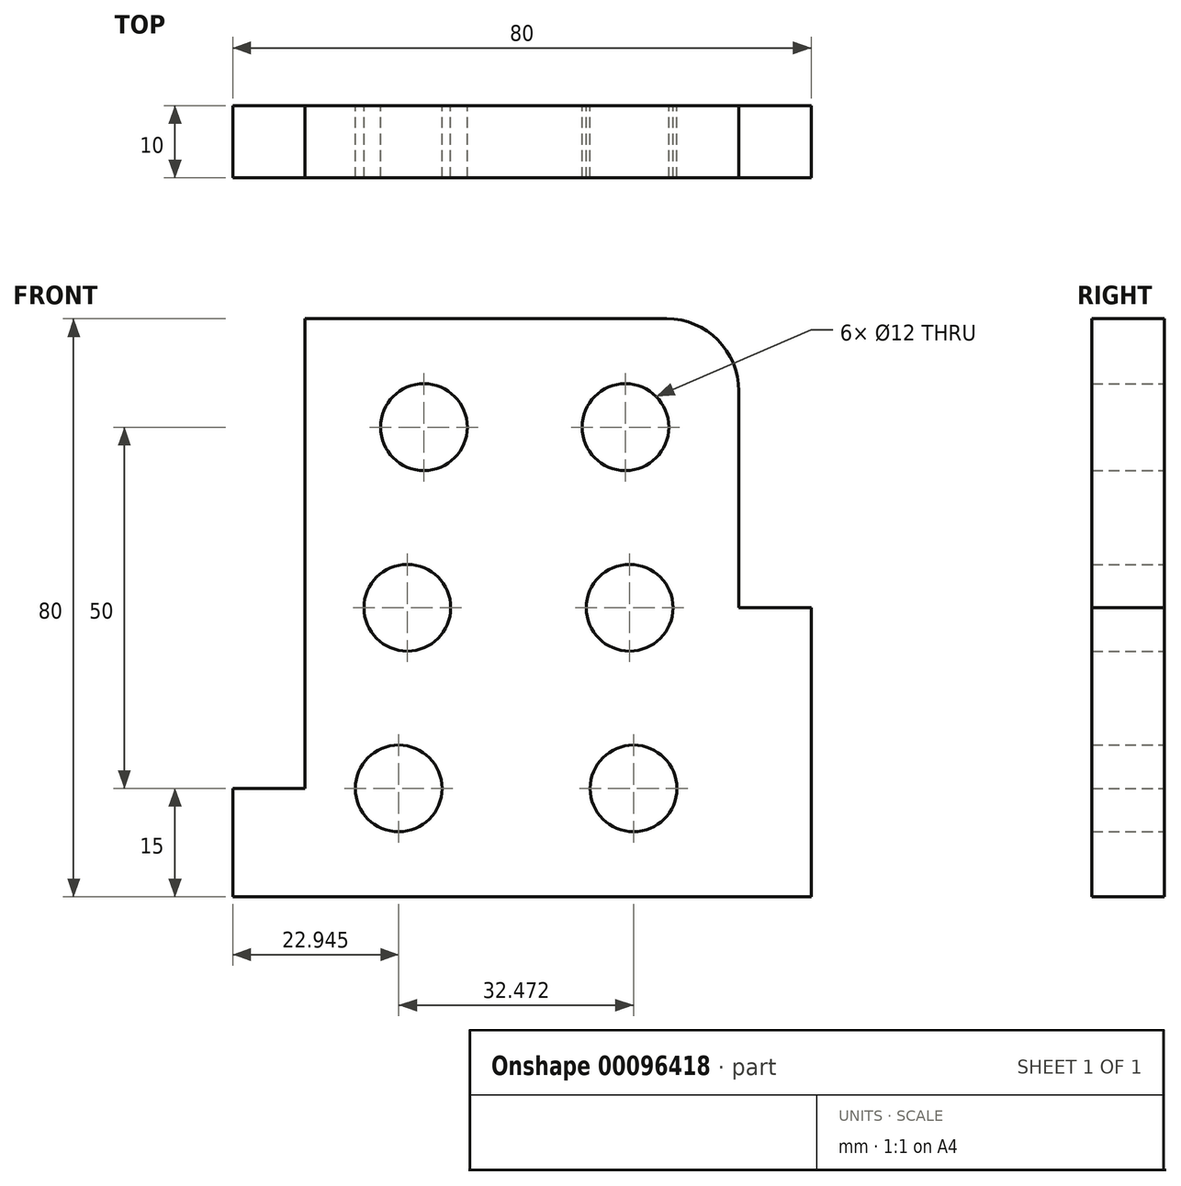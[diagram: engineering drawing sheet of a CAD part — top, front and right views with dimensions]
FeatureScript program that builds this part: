
annotation { "Feature Type Name" : "Feature", "Feature Type Description" : "" }
export const myFeature = defineFeature(function(context is Context, id is Id, definition is map)
    precondition{}
    {
        {
            var Q0;
            Q0=qCreatedBy(makeId("Front.planeOp"),FACE);
            var sketch = newSketch(context, id + "F0", { "sketchPlane" : qUnion([Q0])});
            skLineSegment(sketch, "E0", {"start": v(0, 0) * mm, "end": v(0, 15) * mm});
            skLineSegment(sketch, "E1", {"start": v(0, 15) * mm, "end": v(10, 15) * mm});
            skLineSegment(sketch, "E2", {"start": v(10, 15) * mm, "end": v(10, 80) * mm});
            skLineSegment(sketch, "E3", {"start": v(10, 80) * mm, "end": v(60, 80) * mm});
            skLineSegment(sketch, "E4", {"start": v(70, 70) * mm, "end": v(70, 40) * mm});
            skLineSegment(sketch, "E5", {"start": v(70, 40) * mm, "end": v(80, 40) * mm});
            skLineSegment(sketch, "E6", {"start": v(80, 40) * mm, "end": v(80, 0) * mm});
            skLineSegment(sketch, "E7", {"start": v(80, 0) * mm, "end": v(0, 0) * mm});
            skCircle(sketch, "E8", {"center": v(22.95, 15) * mm, "radius": 6 * mm});
            skCircle(sketch, "E9", {"center": v(55.42, 15) * mm, "radius": 6 * mm});
            skCircle(sketch, "E10", {"center": v(24.14, 40) * mm, "radius": 6 * mm});
            skCircle(sketch, "E11", {"center": v(54.9, 40) * mm, "radius": 6 * mm});
            skCircle(sketch, "E12", {"center": v(26.44, 65) * mm, "radius": 6 * mm});
            skCircle(sketch, "E13", {"center": v(54.3, 65) * mm, "radius": 6 * mm});
            skPoint(sketch, "E14.visualSharp", {"position": v(70, 80) * mm});
            skArc(sketch, "E14.filletArc", {"start": v(70, 70) * mm, "mid": v(67.07, 77.07) * mm, "end": v(60, 80) * mm});
            skSolve(sketch);
        }
        {
            var Q0;
            Q0 = qSketchRegion(id + "F0", true);
            extrude(context, id + "F1", {"entities" : qUnion([Q0]), "depth" : 10 * mm});
        }
    });
